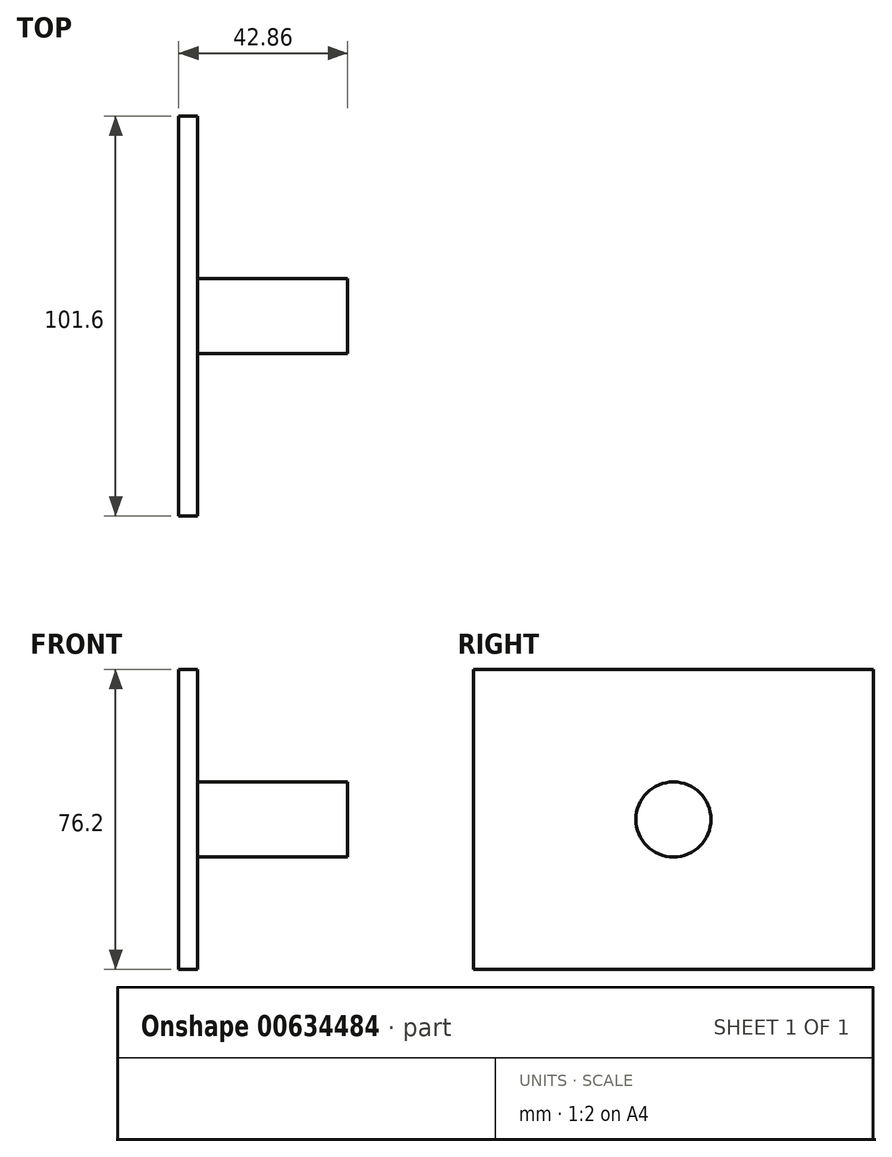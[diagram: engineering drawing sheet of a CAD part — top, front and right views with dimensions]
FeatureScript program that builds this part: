
annotation { "Feature Type Name" : "Feature", "Feature Type Description" : "" }
export const myFeature = defineFeature(function(context is Context, id is Id, definition is map)
    precondition{}
    {
        {
            var Q0;
            Q0=qCreatedBy(makeId("Right.planeOp"),FACE);
            var sketch = newSketch(context, id + "F0", { "sketchPlane" : qUnion([Q0])});
            skLineSegment(sketch, "E0.bottom", {"start": v(0, 0) * mm, "end": v(101.6, 0) * mm});
            skLineSegment(sketch, "E0.top", {"start": v(0, 76.2) * mm, "end": v(101.6, 76.2) * mm});
            skLineSegment(sketch, "E0.left", {"start": v(0, 0) * mm, "end": v(0, 76.2) * mm});
            skLineSegment(sketch, "E0.right", {"start": v(101.6, 0) * mm, "end": v(101.6, 76.2) * mm});
            skSolve(sketch);
        }
        {
            var Q0;
            Q0 = qSketchRegion(id + "F0", true);
            extrude(context, id + "F1", {"entities" : qUnion([Q0]), "depth" : 4.76 * mm, "offsetDistance" : 25.4 * mm});
        }
        {
            var Q0;
            Q0=makeQuery(id+"F1.opExtrude","CAP_FACE",FACE,{"disambiguationData":[OSD([sQuery(id+"F0.wireOp",EDGE,"E0.bottom"),sQuery(id+"F0.wireOp",EDGE,"E0.top"),sQuery(id+"F0.wireOp",EDGE,"E0.left"),sQuery(id+"F0.wireOp",EDGE,"E0.right")])],"isStart":false});
            var sketch = newSketch(context, id + "F2", { "sketchPlane" : qUnion([Q0])});
            skCircle(sketch, "E1", {"center": v(50.8, 38.1) * mm, "radius": 9.53 * mm});
            skPoint(sketch, "E1.centerSnap0", {"position": v(50.8, 0) * mm});
            skPoint(sketch, "E1.centerSnap1", {"position": v(0, 38.1) * mm});
            skSolve(sketch);
        }
        {
            var Q0;
            Q0=makeQuery(id+"F2.imprint","IMPRINT",FACE,{"disambiguationData":[TD([[makeQuery(id+"F2.imprint","IMPRINT",EDGE,{"derivedFrom":sQuery(id+"F2.wireOp",EDGE,"E1")}),1.0]])]});
            extrude(context, id + "F3", {"entities" : qUnion([Q0]), "operationType" : NewBodyOperationType.ADD, "depth" : 38.1 * mm, "offsetDistance" : 25.4 * mm});
        }
    });
